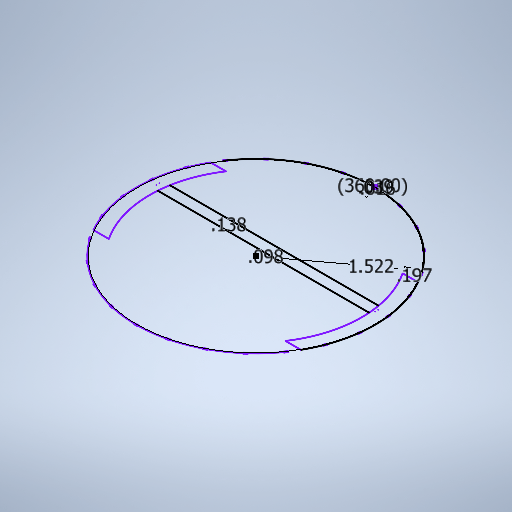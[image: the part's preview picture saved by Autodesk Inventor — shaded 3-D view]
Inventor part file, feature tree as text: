
AUTODESK INVENTOR PART (.ipt)
format: ipt  version: 2025 (Build 290162010, 162A)  size: 306,176 bytes
history: native  units: in
note: dims shown in document units (in); Inventor stores cm internally (conversion verified against a paired STEP export)
features: sketch x2
ambient origin geometry x8: Origin, YZ Plane, XZ Plane, XY Plane, X Axis, Y Axis, Z Axis, Center Point
feature tree (2):
  sketch  "Sketch1"  dims[d0=3.0433in d1=0.1679in]
  sketch  "Sketch Circular Pattern2"  dims[d2=0.0984in d3=0.1378in d10=0.0394in d11=0.0157in d12=10.2362in d14=360.0deg d16=0.5118in d17=0.8465in d18=1.5217in d19=0.1967in]
